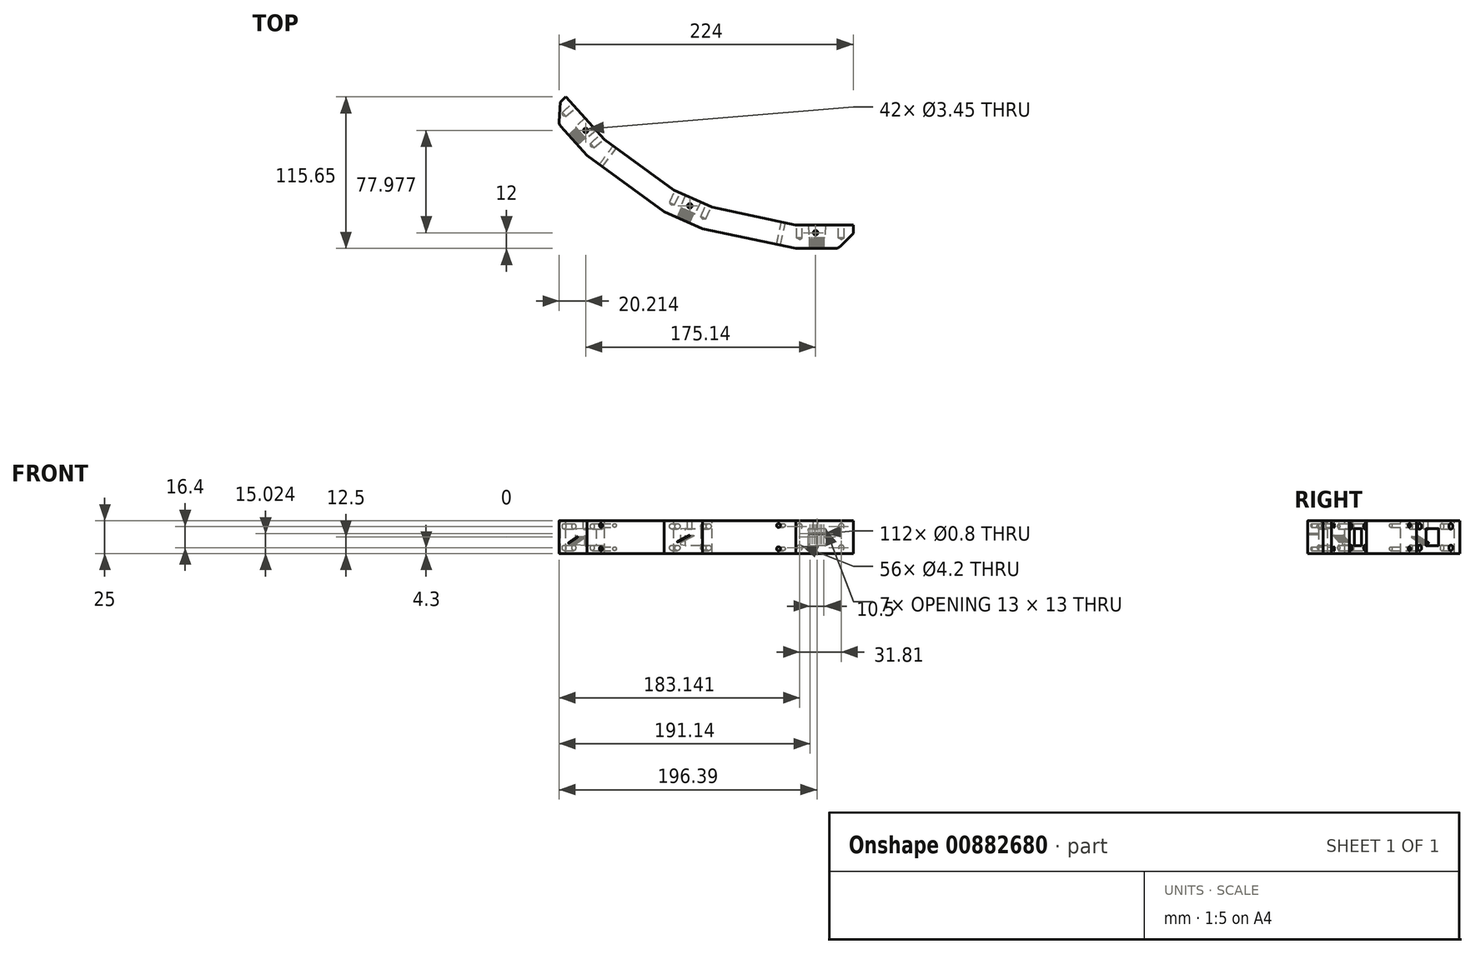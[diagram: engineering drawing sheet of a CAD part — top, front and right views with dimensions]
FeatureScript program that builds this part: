
annotation { "Feature Type Name" : "Feature", "Feature Type Description" : "" }
export const myFeature = defineFeature(function(context is Context, id is Id, definition is map)
    precondition{}
    {
        {
            var Q0;
            Q0=qCreatedBy(makeId("Top.planeOp"),FACE);
            var sketch = newSketch(context, id + "F0", { "sketchPlane" : qUnion([Q0])});
            skCircle(sketch, "E0", {"center": v(0, -260) * mm, "radius": 4.08 * mm});
            skCircle(sketch, "E1", {"center": v(-105.75, -237.52) * mm, "radius": 4.08 * mm});
            skCircle(sketch, "E2", {"center": v(-193.22, -173.97) * mm, "radius": 4.08 * mm});
            skPoint(sketch, "E3", {"position": v(-185.79, -167.28) * mm});
            skPoint(sketch, "E4", {"position": v(-101.68, -228.39) * mm});
            skPoint(sketch, "E5", {"position": v(0, -250) * mm});
            skLineSegment(sketch, "E6.trimOffspring", {"start": v(-104.1, -233.8) * mm, "end": v(-105.75, -237.52) * mm});
            skLineSegment(sketch, "E7.trimOffspring", {"start": v(0, -255.93) * mm, "end": v(0, -260) * mm});
            skLineSegment(sketch, "E8.trimOffspring", {"start": v(-190.19, -171.25) * mm, "end": v(-193.22, -173.97) * mm});
            skLineSegment(sketch, "E9", {"start": v(-185.79, -167.28) * mm, "end": v(-175.08, -179.17) * mm});
            skLineSegment(sketch, "E10", {"start": v(-185.79, -167.28) * mm, "end": v(-195.1, -156.93) * mm});
            skLineSegment(sketch, "E11", {"start": v(-101.68, -228.39) * mm, "end": v(-116.3, -221.88) * mm});
            skLineSegment(sketch, "E12", {"start": v(-101.68, -228.39) * mm, "end": v(-87.07, -234.9) * mm});
            skLineSegment(sketch, "E13", {"start": v(0, -250) * mm, "end": v(-16, -250) * mm});
            skLineSegment(sketch, "E14", {"start": v(0, -250) * mm, "end": v(13.93, -250) * mm});
            skLineSegment(sketch, "E15", {"start": v(-175.08, -179.17) * mm, "end": v(-116.3, -221.88) * mm});
            skLineSegment(sketch, "E16", {"start": v(-87.07, -234.9) * mm, "end": v(-16, -250) * mm});
            skLineSegment(sketch, "E17", {"start": v(-196.38, -153.32) * mm, "end": v(-195.6, -138.3) * mm});
            skLineSegment(sketch, "E18", {"start": v(17.46, -248.54) * mm, "end": v(27.61, -238.39) * mm});
            skPoint(sketch, "E19", {"position": v(-196.5, -155.4) * mm});
            skPoint(sketch, "E20", {"position": v(-172.4, -155.24) * mm});
            skLineSegment(sketch, "E21", {"start": v(-172.4, -155.24) * mm, "end": v(-191.22, -134.35) * mm});
            skLineSegment(sketch, "E22", {"start": v(-195.6, -138.3) * mm, "end": v(-191.22, -134.35) * mm});
            skPoint(sketch, "E23", {"position": v(-94.36, -211.94) * mm});
            skLineSegment(sketch, "E24", {"start": v(-94.36, -211.94) * mm, "end": v(-108.98, -205.43) * mm});
            skLineSegment(sketch, "E25", {"start": v(-172.4, -155.24) * mm, "end": v(-161.7, -167.13) * mm});
            skLineSegment(sketch, "E26", {"start": v(-161.7, -167.13) * mm, "end": v(-108.98, -205.43) * mm});
            skLineSegment(sketch, "E27", {"start": v(-94.36, -211.94) * mm, "end": v(-79.75, -218.45) * mm});
            skPoint(sketch, "E28", {"position": v(-0.5, -232) * mm});
            skLineSegment(sketch, "E29", {"start": v(-0.5, -232) * mm, "end": v(27.61, -232) * mm});
            skLineSegment(sketch, "E30", {"start": v(27.61, -238.39) * mm, "end": v(27.61, -232) * mm});
            skLineSegment(sketch, "E31", {"start": v(-0.5, -232) * mm, "end": v(-16.5, -232) * mm});
            skLineSegment(sketch, "E32", {"start": v(-79.75, -218.45) * mm, "end": v(-16.5, -232) * mm});
            skPoint(sketch, "E33.start.orphan", {"position": v(0, 0) * mm});
            skArc(sketch, "E34.filletArc", {"start": v(-196.38, -153.32) * mm, "mid": v(-196.1, -155.25) * mm, "end": v(-195.1, -156.93) * mm});
            skPoint(sketch, "E35.visualSharp", {"position": v(16, -250) * mm});
            skArc(sketch, "E35.filletArc", {"start": v(13.93, -250) * mm, "mid": v(15.84, -249.62) * mm, "end": v(17.46, -248.54) * mm});
            skSolve(sketch);
        }
        {
            var Q0;
            Q0=makeQuery(id+"F0.imprint","IMPRINT",FACE,{"disambiguationData":[TD([[makeQuery(id+"F0.imprint","IMPRINT",EDGE,{"derivedFrom":sQuery(id+"F0.wireOp",EDGE,"E9")}),1.0]])]});
            extrude(context, id + "F1", {"entities" : qUnion([Q0]), "oppositeDirection" : true, "depth" : 25 * mm, "offsetDistance" : 25 * mm});
        }
        {
            var Q0;
            Q0=makeQuery(id+"F1.opExtrude","SWEPT_FACE",FACE,{"disambiguationData":[OSD([sQuery(id+"F0.wireOp",EDGE,"E24"),sQuery(id+"F0.wireOp",EDGE,"E27")])]});
            var sketch = newSketch(context, id + "F2", { "sketchPlane" : qUnion([Q0])});
            skPoint(sketch, "E36", {"position": v(0, -12.5) * mm});
            skLineSegment(sketch, "E37.bottom", {"start": v(6.5, -19) * mm, "end": v(-6.5, -19) * mm});
            skLineSegment(sketch, "E37.top", {"start": v(6.5, -6) * mm, "end": v(-6.5, -6) * mm});
            skLineSegment(sketch, "E37.left", {"start": v(6.5, -19) * mm, "end": v(6.5, -6) * mm});
            skLineSegment(sketch, "E37.right", {"start": v(-6.5, -19) * mm, "end": v(-6.5, -6) * mm});
            skSolve(sketch);
        }
        {
            var Q0;
            Q0=makeQuery(id+"F2.imprint","IMPRINT",FACE,{"disambiguationData":[TD([[makeQuery(id+"F2.imprint","IMPRINT",EDGE,{"derivedFrom":sQuery(id+"F2.wireOp",EDGE,"E37.bottom")}),-1.0]])]});
            extrude(context, id + "F3", {"entities" : qUnion([Q0]), "operationType" : NewBodyOperationType.REMOVE, "oppositeDirection" : true, "depth" : 10 * mm, "offsetDistance" : 25 * mm, "hasDraft" : true, "draftAngle" : 3 * degree, "draftPullDirection" : true});
        }
        {
            var Q0;
            Q0=makeQuery(id+"F1.opExtrude","SWEPT_FACE",FACE,{"disambiguationData":[OSD([sQuery(id+"F0.wireOp",EDGE,"E21"),sQuery(id+"F0.wireOp",EDGE,"E25")])]});
            var sketch = newSketch(context, id + "F4", { "sketchPlane" : qUnion([Q0])});
            skPoint(sketch, "E38.middle", {"position": v(0, -12.5) * mm});
            skLineSegment(sketch, "E39.bottom", {"start": v(6.5, -19) * mm, "end": v(-6.5, -19) * mm});
            skLineSegment(sketch, "E39.top", {"start": v(6.5, -6) * mm, "end": v(-6.5, -6) * mm});
            skLineSegment(sketch, "E39.left", {"start": v(6.5, -19) * mm, "end": v(6.5, -6) * mm});
            skLineSegment(sketch, "E39.right", {"start": v(-6.5, -19) * mm, "end": v(-6.5, -6) * mm});
            skSolve(sketch);
        }
        {
            var Q0;
            Q0=makeQuery(id+"F4.imprint","IMPRINT",FACE,{"disambiguationData":[TD([[makeQuery(id+"F4.imprint","IMPRINT",EDGE,{"derivedFrom":sQuery(id+"F4.wireOp",EDGE,"E39.bottom")}),-1.0]])]});
            extrude(context, id + "F5", {"entities" : qUnion([Q0]), "operationType" : NewBodyOperationType.REMOVE, "oppositeDirection" : true, "depth" : 10 * mm, "offsetDistance" : 25 * mm, "hasDraft" : true, "draftAngle" : 3 * degree, "draftPullDirection" : true});
        }
        {
            var Q0;
            Q0=makeQuery(id+"F5.boolean.opBoolean","COPY",FACE,{"derivedFrom":makeQuery(id+"F5.opExtrude","CAP_FACE",FACE,{"disambiguationData":[OSD([sQuery(id+"F4.wireOp",EDGE,"E39.bottom"),sQuery(id+"F4.wireOp",EDGE,"E39.top"),sQuery(id+"F4.wireOp",EDGE,"E39.left"),sQuery(id+"F4.wireOp",EDGE,"E39.right")])],"isStart":false})});
            var sketch = newSketch(context, id + "F6", { "sketchPlane" : qUnion([Q0])});
            skLineSegment(sketch, "E40", {"start": v(0, -14.7) * mm, "end": v(6.8, -17.86) * mm});
            skLineSegment(sketch, "E41", {"start": v(0, -14.7) * mm, "end": v(-6.8, -11.53) * mm});
            skPoint(sketch, "E42", {"position": v(0.68, -15.01) * mm});
            skPoint(sketch, "E43", {"position": v(2.04, -15.65) * mm});
            skPoint(sketch, "E44", {"position": v(3.4, -16.28) * mm});
            skPoint(sketch, "E45", {"position": v(4.76, -16.91) * mm});
            skPoint(sketch, "E46", {"position": v(-0.68, -14.38) * mm});
            skPoint(sketch, "E47", {"position": v(-2.04, -13.74) * mm});
            skPoint(sketch, "E48", {"position": v(-3.4, -13.1) * mm});
            skPoint(sketch, "E49", {"position": v(-4.76, -12.48) * mm});
            skLineSegment(sketch, "E50", {"start": v(-4.76, -12.48) * mm, "end": v(-4.76, -18.48) * mm});
            skSolve(sketch);
        }
        {
            var Q0;
            Q0=sQuery(id+"F6.wireOp",VERTEX,"E45");
            var Q1;
            Q1=sQuery(id+"F6.wireOp",VERTEX,"E44");
            var Q2;
            Q2=sQuery(id+"F6.wireOp",VERTEX,"E43");
            var Q3;
            Q3=sQuery(id+"F6.wireOp",VERTEX,"E42");
            var Q4;
            Q4=sQuery(id+"F6.wireOp",VERTEX,"E46");
            var Q5;
            Q5=sQuery(id+"F6.wireOp",VERTEX,"E47");
            var Q6;
            Q6=sQuery(id+"F6.wireOp",VERTEX,"E48");
            var Q7;
            Q7=sQuery(id+"F6.wireOp",VERTEX,"E49");
            var Q8;
            Q8=makeQuery(id+"F1.opExtrude","SWEPT_BODY",BODY,{"disambiguationData":[OSD([sQuery(id+"F0.wireOp",EDGE,"E9"),sQuery(id+"F0.wireOp",EDGE,"E10"),sQuery(id+"F0.wireOp",EDGE,"E11"),sQuery(id+"F0.wireOp",EDGE,"E12"),sQuery(id+"F0.wireOp",EDGE,"E13"),sQuery(id+"F0.wireOp",EDGE,"E14"),sQuery(id+"F0.wireOp",EDGE,"E15"),sQuery(id+"F0.wireOp",EDGE,"E16"),sQuery(id+"F0.wireOp",EDGE,"E17"),sQuery(id+"F0.wireOp",EDGE,"E18"),sQuery(id+"F0.wireOp",EDGE,"E21"),sQuery(id+"F0.wireOp",EDGE,"E22"),sQuery(id+"F0.wireOp",EDGE,"E24"),sQuery(id+"F0.wireOp",EDGE,"E25"),sQuery(id+"F0.wireOp",EDGE,"E26"),sQuery(id+"F0.wireOp",EDGE,"E27"),sQuery(id+"F0.wireOp",EDGE,"E29"),sQuery(id+"F0.wireOp",EDGE,"E30"),sQuery(id+"F0.wireOp",EDGE,"E31"),sQuery(id+"F0.wireOp",EDGE,"E32"),sQuery(id+"F0.wireOp",EDGE,"E34.filletArc"),sQuery(id+"F0.wireOp",EDGE,"E35.filletArc")])]});
            hole(context, id + "F7", {"style" : HoleStyle.C_SINK, "endStyle" : HoleEndStyle.THROUGH, "holeDiameter" : 0.8 * mm, "cSinkDiameter" : 0.87 * mm, "cSinkAngle" : 60 * degree, "majorDiameter" : 5 * mm, "isTappedThrough" : true, "tappedDepth" : 12 * mm, "tapClearance" : 3, "locations" : qUnion([Q0, Q1, Q2, Q3, Q4, Q5, Q6, Q7]), "scope" : qUnion([Q8])});
        }
        {
            var Q0;
            Q0=makeQuery(id+"F3.boolean.opBoolean","COPY",FACE,{"derivedFrom":makeQuery(id+"F3.opExtrude","CAP_FACE",FACE,{"disambiguationData":[OSD([sQuery(id+"F2.wireOp",EDGE,"E37.bottom"),sQuery(id+"F2.wireOp",EDGE,"E37.top"),sQuery(id+"F2.wireOp",EDGE,"E37.left"),sQuery(id+"F2.wireOp",EDGE,"E37.right")])],"isStart":false})});
            var sketch = newSketch(context, id + "F8", { "sketchPlane" : qUnion([Q0])});
            skLineSegment(sketch, "E51", {"start": v(0, -13.7) * mm, "end": v(5.15, -16.1) * mm});
            skLineSegment(sketch, "E52", {"start": v(0, -13.7) * mm, "end": v(-6.8, -10.53) * mm});
            skPoint(sketch, "E53", {"position": v(0.68, -14.01) * mm});
            skPoint(sketch, "E54", {"position": v(2.04, -14.65) * mm});
            skPoint(sketch, "E55", {"position": v(3.4, -15.28) * mm});
            skPoint(sketch, "E56", {"position": v(-0.68, -13.38) * mm});
            skPoint(sketch, "E57", {"position": v(-2.04, -12.74) * mm});
            skPoint(sketch, "E58", {"position": v(-3.4, -12.1) * mm});
            skPoint(sketch, "E59", {"position": v(4.76, -15.91) * mm});
            skPoint(sketch, "E60", {"position": v(-4.76, -11.48) * mm});
            skLineSegment(sketch, "E61", {"start": v(-4.76, -11.48) * mm, "end": v(-4.76, -18.48) * mm});
            skSolve(sketch);
        }
        {
            var Q0;
            Q0=sQuery(id+"F8.wireOp",VERTEX,"E59");
            var Q1;
            Q1=sQuery(id+"F8.wireOp",VERTEX,"E55");
            var Q2;
            Q2=sQuery(id+"F8.wireOp",VERTEX,"E54");
            var Q3;
            Q3=sQuery(id+"F8.wireOp",VERTEX,"E53");
            var Q4;
            Q4=sQuery(id+"F8.wireOp",VERTEX,"E56");
            var Q5;
            Q5=sQuery(id+"F8.wireOp",VERTEX,"E57");
            var Q6;
            Q6=sQuery(id+"F8.wireOp",VERTEX,"E58");
            var Q7;
            Q7=sQuery(id+"F8.wireOp",VERTEX,"E60");
            var Q8;
            Q8=makeQuery(id+"F1.opExtrude","SWEPT_BODY",BODY,{"disambiguationData":[OSD([sQuery(id+"F0.wireOp",EDGE,"E9"),sQuery(id+"F0.wireOp",EDGE,"E10"),sQuery(id+"F0.wireOp",EDGE,"E11"),sQuery(id+"F0.wireOp",EDGE,"E12"),sQuery(id+"F0.wireOp",EDGE,"E13"),sQuery(id+"F0.wireOp",EDGE,"E14"),sQuery(id+"F0.wireOp",EDGE,"E15"),sQuery(id+"F0.wireOp",EDGE,"E16"),sQuery(id+"F0.wireOp",EDGE,"E17"),sQuery(id+"F0.wireOp",EDGE,"E18"),sQuery(id+"F0.wireOp",EDGE,"E21"),sQuery(id+"F0.wireOp",EDGE,"E22"),sQuery(id+"F0.wireOp",EDGE,"E24"),sQuery(id+"F0.wireOp",EDGE,"E25"),sQuery(id+"F0.wireOp",EDGE,"E26"),sQuery(id+"F0.wireOp",EDGE,"E27"),sQuery(id+"F0.wireOp",EDGE,"E29"),sQuery(id+"F0.wireOp",EDGE,"E30"),sQuery(id+"F0.wireOp",EDGE,"E31"),sQuery(id+"F0.wireOp",EDGE,"E32"),sQuery(id+"F0.wireOp",EDGE,"E34.filletArc"),sQuery(id+"F0.wireOp",EDGE,"E35.filletArc")])]});
            hole(context, id + "F9", {"style" : HoleStyle.C_SINK, "endStyle" : HoleEndStyle.THROUGH, "holeDiameter" : 0.8 * mm, "cSinkDiameter" : 0.87 * mm, "cSinkAngle" : 60 * degree, "majorDiameter" : 5 * mm, "isTappedThrough" : true, "tappedDepth" : 12 * mm, "tapClearance" : 3, "locations" : qUnion([Q0, Q1, Q2, Q3, Q4, Q5, Q6, Q7]), "scope" : qUnion([Q8])});
        }
        {
            var Q0;
            Q0=makeQuery(id+"F1.opExtrude","SWEPT_FACE",FACE,{"disambiguationData":[OSD([sQuery(id+"F0.wireOp",EDGE,"E29"),sQuery(id+"F0.wireOp",EDGE,"E31")])]});
            var sketch = newSketch(context, id + "F10", { "sketchPlane" : qUnion([Q0])});
            skLineSegment(sketch, "E62.bottom", {"start": v(6.5, -19) * mm, "end": v(-6.5, -19) * mm});
            skLineSegment(sketch, "E62.top", {"start": v(6.5, -6) * mm, "end": v(-6.5, -6) * mm});
            skLineSegment(sketch, "E62.left", {"start": v(6.5, -19) * mm, "end": v(6.5, -6) * mm});
            skLineSegment(sketch, "E62.right", {"start": v(-6.5, -19) * mm, "end": v(-6.5, -6) * mm});
            skPoint(sketch, "E62.middle", {"position": v(0, -12.5) * mm});
            skSolve(sketch);
        }
        {
            var Q0;
            Q0=makeQuery(id+"F10.imprint","IMPRINT",FACE,{"disambiguationData":[TD([[makeQuery(id+"F10.imprint","IMPRINT",EDGE,{"derivedFrom":sQuery(id+"F10.wireOp",EDGE,"E62.bottom")}),-1.0]])]});
            extrude(context, id + "F11", {"entities" : qUnion([Q0]), "operationType" : NewBodyOperationType.REMOVE, "oppositeDirection" : true, "depth" : 10 * mm, "offsetDistance" : 25 * mm, "hasDraft" : true, "draftAngle" : 3 * degree, "draftPullDirection" : true});
        }
        {
            var Q0;
            Q0=makeQuery(id+"F11.boolean.opBoolean","COPY",FACE,{"derivedFrom":makeQuery(id+"F11.opExtrude","CAP_FACE",FACE,{"disambiguationData":[OSD([sQuery(id+"F10.wireOp",EDGE,"E62.bottom"),sQuery(id+"F10.wireOp",EDGE,"E62.top"),sQuery(id+"F10.wireOp",EDGE,"E62.left"),sQuery(id+"F10.wireOp",EDGE,"E62.right")])],"isStart":false})});
            var sketch = newSketch(context, id + "F12", { "sketchPlane" : qUnion([Q0])});
            skLineSegment(sketch, "E63", {"start": v(0, -18.48) * mm, "end": v(0, -9.98) * mm});
            skPoint(sketch, "E64", {"position": v(0.75, -9.98) * mm});
            skPoint(sketch, "E65", {"position": v(2.25, -9.98) * mm});
            skPoint(sketch, "E66", {"position": v(3.75, -9.98) * mm});
            skPoint(sketch, "E67", {"position": v(5.25, -9.98) * mm});
            skPoint(sketch, "E68", {"position": v(-0.75, -9.98) * mm});
            skPoint(sketch, "E69", {"position": v(-2.25, -9.98) * mm});
            skPoint(sketch, "E70", {"position": v(-3.75, -9.98) * mm});
            skPoint(sketch, "E71", {"position": v(-5.25, -9.98) * mm});
            skSolve(sketch);
        }
        {
            var Q0;
            Q0=sQuery(id+"F12.wireOp",VERTEX,"E67");
            var Q1;
            Q1=sQuery(id+"F12.wireOp",VERTEX,"E66");
            var Q2;
            Q2=sQuery(id+"F12.wireOp",VERTEX,"E65");
            var Q3;
            Q3=sQuery(id+"F12.wireOp",VERTEX,"E64");
            var Q4;
            Q4=sQuery(id+"F12.wireOp",VERTEX,"E68");
            var Q5;
            Q5=sQuery(id+"F12.wireOp",VERTEX,"E69");
            var Q6;
            Q6=sQuery(id+"F12.wireOp",VERTEX,"E70");
            var Q7;
            Q7=sQuery(id+"F12.wireOp",VERTEX,"E71");
            var Q8;
            Q8=makeQuery(id+"F1.opExtrude","SWEPT_BODY",BODY,{"disambiguationData":[OSD([sQuery(id+"F0.wireOp",EDGE,"E9"),sQuery(id+"F0.wireOp",EDGE,"E10"),sQuery(id+"F0.wireOp",EDGE,"E11"),sQuery(id+"F0.wireOp",EDGE,"E12"),sQuery(id+"F0.wireOp",EDGE,"E13"),sQuery(id+"F0.wireOp",EDGE,"E14"),sQuery(id+"F0.wireOp",EDGE,"E15"),sQuery(id+"F0.wireOp",EDGE,"E16"),sQuery(id+"F0.wireOp",EDGE,"E17"),sQuery(id+"F0.wireOp",EDGE,"E18"),sQuery(id+"F0.wireOp",EDGE,"E21"),sQuery(id+"F0.wireOp",EDGE,"E22"),sQuery(id+"F0.wireOp",EDGE,"E24"),sQuery(id+"F0.wireOp",EDGE,"E25"),sQuery(id+"F0.wireOp",EDGE,"E26"),sQuery(id+"F0.wireOp",EDGE,"E27"),sQuery(id+"F0.wireOp",EDGE,"E29"),sQuery(id+"F0.wireOp",EDGE,"E30"),sQuery(id+"F0.wireOp",EDGE,"E31"),sQuery(id+"F0.wireOp",EDGE,"E32"),sQuery(id+"F0.wireOp",EDGE,"E34.filletArc"),sQuery(id+"F0.wireOp",EDGE,"E35.filletArc")])]});
            hole(context, id + "F13", {"style" : HoleStyle.C_SINK, "endStyle" : HoleEndStyle.THROUGH, "holeDiameter" : 0.8 * mm, "cSinkDiameter" : 0.87 * mm, "cSinkAngle" : 60 * degree, "majorDiameter" : 5 * mm, "isTappedThrough" : true, "tappedDepth" : 12 * mm, "tapClearance" : 3, "locations" : qUnion([Q0, Q1, Q2, Q3, Q4, Q5, Q6, Q7]), "scope" : qUnion([Q8])});
        }
        {
            var Q0;
            Q0=makeQuery(id+"F1.opExtrude","CAP_FACE",FACE,{"disambiguationData":[OSD([sQuery(id+"F0.wireOp",EDGE,"E9"),sQuery(id+"F0.wireOp",EDGE,"E10"),sQuery(id+"F0.wireOp",EDGE,"E11"),sQuery(id+"F0.wireOp",EDGE,"E12"),sQuery(id+"F0.wireOp",EDGE,"E13"),sQuery(id+"F0.wireOp",EDGE,"E14"),sQuery(id+"F0.wireOp",EDGE,"E15"),sQuery(id+"F0.wireOp",EDGE,"E16"),sQuery(id+"F0.wireOp",EDGE,"E17"),sQuery(id+"F0.wireOp",EDGE,"E18"),sQuery(id+"F0.wireOp",EDGE,"E21"),sQuery(id+"F0.wireOp",EDGE,"E22"),sQuery(id+"F0.wireOp",EDGE,"E24"),sQuery(id+"F0.wireOp",EDGE,"E25"),sQuery(id+"F0.wireOp",EDGE,"E26"),sQuery(id+"F0.wireOp",EDGE,"E27"),sQuery(id+"F0.wireOp",EDGE,"E29"),sQuery(id+"F0.wireOp",EDGE,"E30"),sQuery(id+"F0.wireOp",EDGE,"E31"),sQuery(id+"F0.wireOp",EDGE,"E32"),sQuery(id+"F0.wireOp",EDGE,"E34.filletArc"),sQuery(id+"F0.wireOp",EDGE,"E35.filletArc")])],"isStart":true});
            var sketch = newSketch(context, id + "F14", { "sketchPlane" : qUnion([Q0])});
            skLineSegment(sketch, "E72", {"start": v(-94.36, -211.94) * mm, "end": v(-101.68, -228.39) * mm});
            skLineSegment(sketch, "E73", {"start": v(-185.1, -168.05) * mm, "end": v(-171.72, -156) * mm});
            skLineSegment(sketch, "E74", {"start": v(-1.04, -250) * mm, "end": v(-1.04, -232) * mm});
            skPoint(sketch, "E75", {"position": v(-1.04, -238) * mm});
            skPoint(sketch, "E76", {"position": v(-96.8, -217.42) * mm});
            skPoint(sketch, "E77", {"position": v(-176.18, -160.02) * mm});
            skSolve(sketch);
        }
        {
            var Q0;
            Q0=sQuery(id+"F14.wireOp",VERTEX,"E77");
            var Q1;
            Q1=sQuery(id+"F14.wireOp",VERTEX,"E76");
            var Q2;
            Q2=sQuery(id+"F14.wireOp",VERTEX,"E75");
            var Q3;
            Q3=makeQuery(id+"F1.opExtrude","SWEPT_BODY",BODY,{"disambiguationData":[OSD([sQuery(id+"F0.wireOp",EDGE,"E9"),sQuery(id+"F0.wireOp",EDGE,"E10"),sQuery(id+"F0.wireOp",EDGE,"E11"),sQuery(id+"F0.wireOp",EDGE,"E12"),sQuery(id+"F0.wireOp",EDGE,"E13"),sQuery(id+"F0.wireOp",EDGE,"E14"),sQuery(id+"F0.wireOp",EDGE,"E15"),sQuery(id+"F0.wireOp",EDGE,"E16"),sQuery(id+"F0.wireOp",EDGE,"E17"),sQuery(id+"F0.wireOp",EDGE,"E18"),sQuery(id+"F0.wireOp",EDGE,"E21"),sQuery(id+"F0.wireOp",EDGE,"E22"),sQuery(id+"F0.wireOp",EDGE,"E24"),sQuery(id+"F0.wireOp",EDGE,"E25"),sQuery(id+"F0.wireOp",EDGE,"E26"),sQuery(id+"F0.wireOp",EDGE,"E27"),sQuery(id+"F0.wireOp",EDGE,"E29"),sQuery(id+"F0.wireOp",EDGE,"E30"),sQuery(id+"F0.wireOp",EDGE,"E31"),sQuery(id+"F0.wireOp",EDGE,"E32"),sQuery(id+"F0.wireOp",EDGE,"E34.filletArc"),sQuery(id+"F0.wireOp",EDGE,"E35.filletArc")])]});
            hole(context, id + "F15", {"style" : HoleStyle.SIMPLE, "endStyle" : HoleEndStyle.BLIND, "standardTappedOrClearance" : lookupTablePath({ "standard" : "ANSI", "engagement" : "75%", "pitch" : "32 tpi", "size" : "#8", "type" : "Tapped" }), "standardBlindInLast" : lookupTablePath({ "standard" : "ANSI", "engagement" : "75%", "pitch" : "32 tpi", "size" : "#8", "type" : "Tapped" }), "holeDiameter" : 3.45 * mm, "majorDiameter" : 4.17 * mm, "showTappedDepth" : true, "holeDepth" : 14.38 * mm, "isTappedThrough" : true, "tappedDepth" : 12 * mm, "tapClearance" : 3, "locations" : qUnion([Q0, Q1, Q2]), "scope" : qUnion([Q3])});
        }
        {
            var Q0;
            {var subQ3=sQuery(id+"F0.wireOp",EDGE,"E31");var subQ4=sQuery(id+"F0.wireOp",EDGE,"E30");var subQ5=sQuery(id+"F0.wireOp",EDGE,"E29");Q0=makeQuery(id+"Fe6iQ39P3XZATja_1.boolean.opBoolean","SPLIT",FACE,{"disambiguationData":[TD([makeQuery(id+"F1.opExtrude","SWEPT_FACE",FACE,{"disambiguationData":[OSD([subQ4])]})])],"derivedFrom":makeQuery(id+"F1.opExtrude","SWEPT_FACE",FACE,{"disambiguationData":[OSD([subQ5,subQ3])]})});}
            var sketch = newSketch(context, id + "F16", { "sketchPlane" : qUnion([Q0])});
            skLineSegment(sketch, "E78", {"start": v(-18.56, -4.3) * mm, "end": v(-27.61, -4.3) * mm});
            skLineSegment(sketch, "E79", {"start": v(-18.56, -20.7) * mm, "end": v(-27.61, -20.7) * mm});
            skPoint(sketch, "E80", {"position": v(13.25, -4.3) * mm});
            skPoint(sketch, "E81", {"position": v(13.25, -20.7) * mm});
            skPoint(sketch, "E82", {"position": v(-18.56, -4.3) * mm});
            skPoint(sketch, "E83", {"position": v(-18.56, -20.7) * mm});
            skSolve(sketch);
        }
        {
            var Q0;
            Q0=sQuery(id+"F16.wireOp",VERTEX,"960df98d-92ac-47f4-9385-bcb4d4738518");
            var Q1;
            Q1=sQuery(id+"F16.wireOp",VERTEX,"E80");
            var Q2;
            Q2=sQuery(id+"F16.wireOp",VERTEX,"E81");
            var Q3;
            Q3=sQuery(id+"F16.wireOp",VERTEX,"70c8c2b4-ec63-4f9a-a490-eeb2e280e894");
            var Q4;
            Q4=sQuery(id+"F16.wireOp",VERTEX,"E82");
            var Q5;
            Q5=sQuery(id+"F16.wireOp",VERTEX,"E83");
            var Q6;
            Q6=makeQuery(id+"F1.opExtrude","SWEPT_BODY",BODY,{"disambiguationData":[OSD([sQuery(id+"F0.wireOp",EDGE,"E9"),sQuery(id+"F0.wireOp",EDGE,"E10"),sQuery(id+"F0.wireOp",EDGE,"E11"),sQuery(id+"F0.wireOp",EDGE,"E12"),sQuery(id+"F0.wireOp",EDGE,"E13"),sQuery(id+"F0.wireOp",EDGE,"E14"),sQuery(id+"F0.wireOp",EDGE,"E15"),sQuery(id+"F0.wireOp",EDGE,"E16"),sQuery(id+"F0.wireOp",EDGE,"E17"),sQuery(id+"F0.wireOp",EDGE,"E18"),sQuery(id+"F0.wireOp",EDGE,"E21"),sQuery(id+"F0.wireOp",EDGE,"E22"),sQuery(id+"F0.wireOp",EDGE,"E24"),sQuery(id+"F0.wireOp",EDGE,"E25"),sQuery(id+"F0.wireOp",EDGE,"E26"),sQuery(id+"F0.wireOp",EDGE,"E27"),sQuery(id+"F0.wireOp",EDGE,"E29"),sQuery(id+"F0.wireOp",EDGE,"E30"),sQuery(id+"F0.wireOp",EDGE,"E31"),sQuery(id+"F0.wireOp",EDGE,"E32"),sQuery(id+"F0.wireOp",EDGE,"E34.filletArc"),sQuery(id+"F0.wireOp",EDGE,"E35.filletArc")])]});
            hole(context, id + "F17", {"style" : HoleStyle.SIMPLE, "endStyle" : HoleEndStyle.BLIND, "standardTappedOrClearance" : lookupTablePath({ "standard" : "ISO", "engagement" : "75%", "pitch" : "0.8 mm", "size" : "M5", "type" : "Tapped" }), "standardBlindInLast" : lookupTablePath({ "standard" : "ISO", "engagement" : "75%", "pitch" : "0.8 mm", "size" : "M5", "type" : "Tapped" }), "holeDiameter" : 4.2 * mm, "majorDiameter" : 5 * mm, "showTappedDepth" : true, "holeDepth" : 10 * mm, "isTappedThrough" : true, "tappedDepth" : 7.6 * mm, "tapClearance" : 3, "locations" : qUnion([Q0, Q1, Q2, Q3, Q4, Q5]), "scope" : qUnion([Q6])});
        }
        {
            var Q0;
            Q0=makeQuery(id+"F11.boolean.opBoolean","COPY",EDGE,{"derivedFrom":makeQuery(id+"F11.opExtrude","CAP_EDGE",EDGE,{"disambiguationData":[OSD([sQuery(id+"F10.wireOp",EDGE,"E62.left")])],"isStart":false})});
            var Q1;
            Q1=makeQuery(id+"F11.boolean.opBoolean","COPY",EDGE,{"derivedFrom":makeQuery(id+"F11.opExtrude","CAP_EDGE",EDGE,{"disambiguationData":[OSD([sQuery(id+"F10.wireOp",EDGE,"E62.top")])],"isStart":false})});
            var Q2;
            Q2=makeQuery(id+"F11.boolean.opBoolean","COPY",EDGE,{"derivedFrom":makeQuery(id+"F11.opExtrude","CAP_EDGE",EDGE,{"disambiguationData":[OSD([sQuery(id+"F10.wireOp",EDGE,"E62.right")])],"isStart":false})});
            var Q3;
            Q3=makeQuery(id+"F11.boolean.opBoolean","COPY",EDGE,{"derivedFrom":makeQuery(id+"F11.opExtrude","CAP_EDGE",EDGE,{"disambiguationData":[OSD([sQuery(id+"F10.wireOp",EDGE,"E62.bottom")])],"isStart":false})});
            var Q4;
            Q4=makeQuery(id+"F11.boolean.opBoolean","COPY",EDGE,{"derivedFrom":makeQuery(id+"F11.opExtrude","SWEPT_EDGE",EDGE,{"disambiguationData":[OSD([sQuery(id+"F10.wireOp",EDGE,"E62.top"),sQuery(id+"F10.wireOp",EDGE,"E62.left")])]})});
            var Q5;
            Q5=makeQuery(id+"F11.boolean.opBoolean","COPY",EDGE,{"derivedFrom":makeQuery(id+"F11.opExtrude","SWEPT_EDGE",EDGE,{"disambiguationData":[OSD([sQuery(id+"F10.wireOp",EDGE,"E62.top"),sQuery(id+"F10.wireOp",EDGE,"E62.right")])]})});
            var Q6;
            Q6=makeQuery(id+"F11.boolean.opBoolean","COPY",EDGE,{"derivedFrom":makeQuery(id+"F11.opExtrude","SWEPT_EDGE",EDGE,{"disambiguationData":[OSD([sQuery(id+"F10.wireOp",EDGE,"E62.bottom"),sQuery(id+"F10.wireOp",EDGE,"E62.right")])]})});
            fillet(context, id + "F18", {"entities" : qUnion([Q0, Q1, Q2, Q3, Q4, Q5, Q6]), "radius" : 0.3 * mm, "tangentPropagation" : true, "allowEdgeOverflow" : false});
        }
        {
            var Q0;
            Q0=makeQuery(id+"F3.boolean.opBoolean","COPY",EDGE,{"derivedFrom":makeQuery(id+"F3.opExtrude","CAP_EDGE",EDGE,{"disambiguationData":[OSD([sQuery(id+"F2.wireOp",EDGE,"E37.top")])],"isStart":false})});
            var Q1;
            Q1=makeQuery(id+"F3.boolean.opBoolean","COPY",EDGE,{"derivedFrom":makeQuery(id+"F3.opExtrude","CAP_EDGE",EDGE,{"disambiguationData":[OSD([sQuery(id+"F2.wireOp",EDGE,"E37.right")])],"isStart":false})});
            var Q2;
            Q2=makeQuery(id+"F3.boolean.opBoolean","COPY",EDGE,{"derivedFrom":makeQuery(id+"F3.opExtrude","SWEPT_EDGE",EDGE,{"disambiguationData":[OSD([sQuery(id+"F2.wireOp",EDGE,"E37.top"),sQuery(id+"F2.wireOp",EDGE,"E37.right")])]})});
            var Q3;
            Q3=makeQuery(id+"F3.boolean.opBoolean","COPY",EDGE,{"derivedFrom":makeQuery(id+"F3.opExtrude","SWEPT_EDGE",EDGE,{"disambiguationData":[OSD([sQuery(id+"F2.wireOp",EDGE,"E37.bottom"),sQuery(id+"F2.wireOp",EDGE,"E37.right")])]})});
            var Q4;
            Q4=makeQuery(id+"F3.boolean.opBoolean","COPY",EDGE,{"derivedFrom":makeQuery(id+"F3.opExtrude","CAP_EDGE",EDGE,{"disambiguationData":[OSD([sQuery(id+"F2.wireOp",EDGE,"E37.bottom")])],"isStart":false})});
            var Q5;
            Q5=makeQuery(id+"F3.boolean.opBoolean","COPY",EDGE,{"derivedFrom":makeQuery(id+"F3.opExtrude","CAP_EDGE",EDGE,{"disambiguationData":[OSD([sQuery(id+"F2.wireOp",EDGE,"E37.left")])],"isStart":false})});
            var Q6;
            Q6=makeQuery(id+"F3.boolean.opBoolean","COPY",EDGE,{"derivedFrom":makeQuery(id+"F3.opExtrude","SWEPT_EDGE",EDGE,{"disambiguationData":[OSD([sQuery(id+"F2.wireOp",EDGE,"E37.top"),sQuery(id+"F2.wireOp",EDGE,"E37.left")])]})});
            var Q7;
            Q7=makeQuery(id+"F3.boolean.opBoolean","COPY",EDGE,{"derivedFrom":makeQuery(id+"F3.opExtrude","SWEPT_EDGE",EDGE,{"disambiguationData":[OSD([sQuery(id+"F2.wireOp",EDGE,"E37.bottom"),sQuery(id+"F2.wireOp",EDGE,"E37.left")])]})});
            fillet(context, id + "F19", {"entities" : qUnion([Q0, Q1, Q2, Q3, Q4, Q5, Q6, Q7]), "radius" : 0.3 * mm, "tangentPropagation" : true, "allowEdgeOverflow" : false});
        }
        {
            var Q0;
            Q0=makeQuery(id+"F5.boolean.opBoolean","COPY",EDGE,{"derivedFrom":makeQuery(id+"F5.opExtrude","CAP_EDGE",EDGE,{"disambiguationData":[OSD([sQuery(id+"F4.wireOp",EDGE,"E39.bottom")])],"isStart":false})});
            var Q1;
            Q1=makeQuery(id+"F5.boolean.opBoolean","COPY",EDGE,{"derivedFrom":makeQuery(id+"F5.opExtrude","CAP_EDGE",EDGE,{"disambiguationData":[OSD([sQuery(id+"F4.wireOp",EDGE,"E39.top")])],"isStart":false})});
            var Q2;
            Q2=makeQuery(id+"F5.boolean.opBoolean","COPY",EDGE,{"derivedFrom":makeQuery(id+"F5.opExtrude","CAP_EDGE",EDGE,{"disambiguationData":[OSD([sQuery(id+"F4.wireOp",EDGE,"E39.right")])],"isStart":false})});
            var Q3;
            Q3=makeQuery(id+"F5.boolean.opBoolean","COPY",EDGE,{"derivedFrom":makeQuery(id+"F5.opExtrude","SWEPT_EDGE",EDGE,{"disambiguationData":[OSD([sQuery(id+"F4.wireOp",EDGE,"E39.top"),sQuery(id+"F4.wireOp",EDGE,"E39.right")])]})});
            var Q4;
            Q4=makeQuery(id+"F5.boolean.opBoolean","COPY",EDGE,{"derivedFrom":makeQuery(id+"F5.opExtrude","SWEPT_EDGE",EDGE,{"disambiguationData":[OSD([sQuery(id+"F4.wireOp",EDGE,"E39.bottom"),sQuery(id+"F4.wireOp",EDGE,"E39.right")])]})});
            var Q5;
            Q5=makeQuery(id+"F5.boolean.opBoolean","COPY",EDGE,{"derivedFrom":makeQuery(id+"F5.opExtrude","CAP_EDGE",EDGE,{"disambiguationData":[OSD([sQuery(id+"F4.wireOp",EDGE,"E39.left")])],"isStart":false})});
            var Q6;
            Q6=makeQuery(id+"F5.boolean.opBoolean","COPY",EDGE,{"derivedFrom":makeQuery(id+"F5.opExtrude","SWEPT_EDGE",EDGE,{"disambiguationData":[OSD([sQuery(id+"F4.wireOp",EDGE,"E39.top"),sQuery(id+"F4.wireOp",EDGE,"E39.left")])]})});
            var Q7;
            Q7=makeQuery(id+"F5.boolean.opBoolean","COPY",EDGE,{"derivedFrom":makeQuery(id+"F5.opExtrude","SWEPT_EDGE",EDGE,{"disambiguationData":[OSD([sQuery(id+"F4.wireOp",EDGE,"E39.bottom"),sQuery(id+"F4.wireOp",EDGE,"E39.left")])]})});
            fillet(context, id + "F20", {"entities" : qUnion([Q0, Q1, Q2, Q3, Q4, Q5, Q6, Q7]), "radius" : 0.3 * mm, "tangentPropagation" : true, "allowEdgeOverflow" : false});
        }
        {
            var Q0;
            {var subQ6=sQuery(id+"F0.wireOp",EDGE,"E27");var subQ7=sQuery(id+"F0.wireOp",EDGE,"E26");var subQ9=sQuery(id+"F0.wireOp",EDGE,"E24");Q0=makeQuery(id+"Fw17XcnKaz8ayvf_1.boolean.opBoolean","SPLIT",FACE,{"disambiguationData":[TD([makeQuery(id+"F1.opExtrude","SWEPT_FACE",FACE,{"disambiguationData":[OSD([subQ7])]})])],"derivedFrom":makeQuery(id+"F1.opExtrude","SWEPT_FACE",FACE,{"disambiguationData":[OSD([subQ9,subQ6])]})});}
            var sketch = newSketch(context, id + "F21", { "sketchPlane" : qUnion([Q0])});
            skPoint(sketch, "E84", {"position": v(-13, -4.3) * mm});
            skPoint(sketch, "E85", {"position": v(-13, -20.7) * mm});
            skPoint(sketch, "E86", {"position": v(13, -4.3) * mm});
            skPoint(sketch, "E87", {"position": v(13, -20.7) * mm});
            skPoint(sketch, "E88.orphan", {"position": v(-10, -4.3) * mm});
            skPoint(sketch, "E89.orphan", {"position": v(10, -4.3) * mm});
            skPoint(sketch, "E90.orphan", {"position": v(-10, -20.7) * mm});
            skPoint(sketch, "E91.orphan", {"position": v(10, -20.7) * mm});
            skPoint(sketch, "E92.end.orphan", {"position": v(16, -4.3) * mm});
            skPoint(sketch, "E93.end.orphan", {"position": v(16, -20.7) * mm});
            skPoint(sketch, "E94.end.orphan", {"position": v(-16, -4.3) * mm});
            skPoint(sketch, "E95.end.orphan", {"position": v(-16, -20.7) * mm});
            skSolve(sketch);
        }
        {
            var Q0;
            Q0=sQuery(id+"F21.wireOp",VERTEX,"E84");
            var Q1;
            Q1=sQuery(id+"F21.wireOp",VERTEX,"E85");
            var Q2;
            Q2=sQuery(id+"F21.wireOp",VERTEX,"E86");
            var Q3;
            Q3=sQuery(id+"F21.wireOp",VERTEX,"E87");
            var Q4;
            Q4=makeQuery(id+"F1.opExtrude","SWEPT_BODY",BODY,{"disambiguationData":[OSD([sQuery(id+"F0.wireOp",EDGE,"E9"),sQuery(id+"F0.wireOp",EDGE,"E10"),sQuery(id+"F0.wireOp",EDGE,"E11"),sQuery(id+"F0.wireOp",EDGE,"E12"),sQuery(id+"F0.wireOp",EDGE,"E13"),sQuery(id+"F0.wireOp",EDGE,"E14"),sQuery(id+"F0.wireOp",EDGE,"E15"),sQuery(id+"F0.wireOp",EDGE,"E16"),sQuery(id+"F0.wireOp",EDGE,"E17"),sQuery(id+"F0.wireOp",EDGE,"E18"),sQuery(id+"F0.wireOp",EDGE,"E21"),sQuery(id+"F0.wireOp",EDGE,"E22"),sQuery(id+"F0.wireOp",EDGE,"E24"),sQuery(id+"F0.wireOp",EDGE,"E25"),sQuery(id+"F0.wireOp",EDGE,"E26"),sQuery(id+"F0.wireOp",EDGE,"E27"),sQuery(id+"F0.wireOp",EDGE,"E29"),sQuery(id+"F0.wireOp",EDGE,"E30"),sQuery(id+"F0.wireOp",EDGE,"E31"),sQuery(id+"F0.wireOp",EDGE,"E32"),sQuery(id+"F0.wireOp",EDGE,"E34.filletArc"),sQuery(id+"F0.wireOp",EDGE,"E35.filletArc")])]});
            hole(context, id + "F22", {"style" : HoleStyle.SIMPLE, "endStyle" : HoleEndStyle.BLIND, "standardTappedOrClearance" : lookupTablePath({ "standard" : "ISO", "engagement" : "75%", "pitch" : "0.8 mm", "size" : "M5", "type" : "Tapped" }), "standardBlindInLast" : lookupTablePath({ "standard" : "ISO", "engagement" : "75%", "pitch" : "0.8 mm", "size" : "M5", "type" : "Tapped" }), "holeDiameter" : 4.2 * mm, "majorDiameter" : 5 * mm, "showTappedDepth" : true, "holeDepth" : 10 * mm, "isTappedThrough" : true, "tappedDepth" : 7.6 * mm, "tapClearance" : 3, "locations" : qUnion([Q0, Q1, Q2, Q3]), "scope" : qUnion([Q4])});
        }
        {
            var Q0;
            {var subQ0=sQuery(id+"F0.wireOp",EDGE,"E22");var subQ9=sQuery(id+"F0.wireOp",EDGE,"E25");var subQ11=sQuery(id+"F0.wireOp",EDGE,"E21");Q0=makeQuery(id+"FjpGXXQrmrtnJyJ_1.boolean.opBoolean","SPLIT",FACE,{"disambiguationData":[TD([makeQuery(id+"F1.opExtrude","SWEPT_FACE",FACE,{"disambiguationData":[OSD([subQ0])]})])],"derivedFrom":makeQuery(id+"F1.opExtrude","SWEPT_FACE",FACE,{"disambiguationData":[OSD([subQ11,subQ9])]})});}
            var sketch = newSketch(context, id + "F23", { "sketchPlane" : qUnion([Q0])});
            skLineSegment(sketch, "E96", {"start": v(19.06, -4.3) * mm, "end": v(28.1, -4.3) * mm});
            skLineSegment(sketch, "E97", {"start": v(19.06, -20.7) * mm, "end": v(28.1, -20.7) * mm});
            skPoint(sketch, "E98", {"position": v(-13, -4.3) * mm});
            skPoint(sketch, "E99", {"position": v(-13, -20.7) * mm});
            skPoint(sketch, "E100", {"position": v(19.06, -4.3) * mm});
            skPoint(sketch, "E101", {"position": v(19.06, -20.7) * mm});
            skPoint(sketch, "E102.orphan", {"position": v(-10, -20.7) * mm});
            skPoint(sketch, "E103.orphan", {"position": v(-10, -4.3) * mm});
            skPoint(sketch, "E104.end.orphan", {"position": v(-16, -20.7) * mm});
            skPoint(sketch, "E105.end.orphan", {"position": v(-16, -4.3) * mm});
            skSolve(sketch);
        }
        {
            var Q0;
            Q0=sQuery(id+"F23.wireOp",VERTEX,"E98");
            var Q1;
            Q1=sQuery(id+"F23.wireOp",VERTEX,"E99");
            var Q2;
            Q2=sQuery(id+"F23.wireOp",VERTEX,"95fecb40-6dee-438e-ade6-2e9aa052387a");
            var Q3;
            Q3=sQuery(id+"F23.wireOp",VERTEX,"5c4d115d-a3d0-4a2b-9813-a859292176f2");
            var Q4;
            Q4=sQuery(id+"F23.wireOp",VERTEX,"E100");
            var Q5;
            Q5=sQuery(id+"F23.wireOp",VERTEX,"E101");
            var Q6;
            Q6=makeQuery(id+"F1.opExtrude","SWEPT_BODY",BODY,{"disambiguationData":[OSD([sQuery(id+"F0.wireOp",EDGE,"E9"),sQuery(id+"F0.wireOp",EDGE,"E10"),sQuery(id+"F0.wireOp",EDGE,"E11"),sQuery(id+"F0.wireOp",EDGE,"E12"),sQuery(id+"F0.wireOp",EDGE,"E13"),sQuery(id+"F0.wireOp",EDGE,"E14"),sQuery(id+"F0.wireOp",EDGE,"E15"),sQuery(id+"F0.wireOp",EDGE,"E16"),sQuery(id+"F0.wireOp",EDGE,"E17"),sQuery(id+"F0.wireOp",EDGE,"E18"),sQuery(id+"F0.wireOp",EDGE,"E21"),sQuery(id+"F0.wireOp",EDGE,"E22"),sQuery(id+"F0.wireOp",EDGE,"E24"),sQuery(id+"F0.wireOp",EDGE,"E25"),sQuery(id+"F0.wireOp",EDGE,"E26"),sQuery(id+"F0.wireOp",EDGE,"E27"),sQuery(id+"F0.wireOp",EDGE,"E29"),sQuery(id+"F0.wireOp",EDGE,"E30"),sQuery(id+"F0.wireOp",EDGE,"E31"),sQuery(id+"F0.wireOp",EDGE,"E32"),sQuery(id+"F0.wireOp",EDGE,"E34.filletArc"),sQuery(id+"F0.wireOp",EDGE,"E35.filletArc")])]});
            hole(context, id + "F24", {"style" : HoleStyle.SIMPLE, "endStyle" : HoleEndStyle.BLIND, "standardTappedOrClearance" : lookupTablePath({ "standard" : "ISO", "engagement" : "75%", "pitch" : "0.8 mm", "size" : "M5", "type" : "Tapped" }), "standardBlindInLast" : lookupTablePath({ "standard" : "ISO", "engagement" : "75%", "pitch" : "0.8 mm", "size" : "M5", "type" : "Tapped" }), "holeDiameter" : 4.2 * mm, "majorDiameter" : 5 * mm, "showTappedDepth" : true, "holeDepth" : 10 * mm, "isTappedThrough" : true, "tappedDepth" : 7.6 * mm, "tapClearance" : 3, "locations" : qUnion([Q0, Q1, Q2, Q3, Q4, Q5]), "scope" : qUnion([Q6])});
        }
        {
            var Q0;
            Q0=makeQuery(id+"F1.opExtrude","SWEPT_FACE",FACE,{"disambiguationData":[OSD([sQuery(id+"F0.wireOp",EDGE,"E32")])]});
            var sketch = newSketch(context, id + "F25", { "sketchPlane" : qUnion([Q0])});
            skLineSegment(sketch, "E106", {"start": v(-32.47, 0) * mm, "end": v(32.22, -25) * mm});
            skLineSegment(sketch, "E107", {"start": v(-32.47, -25) * mm, "end": v(32.22, 0) * mm});
            skPoint(sketch, "E108", {"position": v(-23.14, -21.4) * mm});
            skPoint(sketch, "E109", {"position": v(-23.14, -3.6) * mm});
            skPoint(sketch, "E110", {"position": v(32.22, -25) * mm});
            skSolve(sketch);
        }
        {
            var Q0;
            Q0=sQuery(id+"F25.wireOp",VERTEX,"E109");
            var Q1;
            Q1=sQuery(id+"F25.wireOp",VERTEX,"E108");
            var Q2;
            Q2=sQuery(id+"F25.wireOp",VERTEX,"c15fa140-9604-4616-bb4b-56b4743ac27f");
            var Q3;
            Q3=sQuery(id+"F25.wireOp",VERTEX,"ee11ad6e-ffd4-4928-85d1-b1639c15d129");
            var Q4;
            Q4=makeQuery(id+"F1.opExtrude","SWEPT_BODY",BODY,{"disambiguationData":[OSD([sQuery(id+"F0.wireOp",EDGE,"E9"),sQuery(id+"F0.wireOp",EDGE,"E10"),sQuery(id+"F0.wireOp",EDGE,"E11"),sQuery(id+"F0.wireOp",EDGE,"E12"),sQuery(id+"F0.wireOp",EDGE,"E13"),sQuery(id+"F0.wireOp",EDGE,"E14"),sQuery(id+"F0.wireOp",EDGE,"E15"),sQuery(id+"F0.wireOp",EDGE,"E16"),sQuery(id+"F0.wireOp",EDGE,"E17"),sQuery(id+"F0.wireOp",EDGE,"E18"),sQuery(id+"F0.wireOp",EDGE,"E21"),sQuery(id+"F0.wireOp",EDGE,"E22"),sQuery(id+"F0.wireOp",EDGE,"E24"),sQuery(id+"F0.wireOp",EDGE,"E25"),sQuery(id+"F0.wireOp",EDGE,"E26"),sQuery(id+"F0.wireOp",EDGE,"E27"),sQuery(id+"F0.wireOp",EDGE,"E29"),sQuery(id+"F0.wireOp",EDGE,"E30"),sQuery(id+"F0.wireOp",EDGE,"E31"),sQuery(id+"F0.wireOp",EDGE,"E32"),sQuery(id+"F0.wireOp",EDGE,"E34.filletArc"),sQuery(id+"F0.wireOp",EDGE,"E35.filletArc")])]});
            hole(context, id + "F26", {"style" : HoleStyle.SIMPLE, "endStyle" : HoleEndStyle.THROUGH, "holeDiameter" : 3.02 * mm, "majorDiameter" : 5 * mm, "isTappedThrough" : true, "tappedDepth" : 7.6 * mm, "tapClearance" : 3, "locations" : qUnion([Q0, Q1, Q2, Q3]), "scope" : qUnion([Q4])});
        }
        {
            var Q0;
            Q0=makeQuery(id+"F1.opExtrude","SWEPT_FACE",FACE,{"disambiguationData":[OSD([sQuery(id+"F0.wireOp",EDGE,"E26")])]});
            var sketch = newSketch(context, id + "F27", { "sketchPlane" : qUnion([Q0])});
            skLineSegment(sketch, "E111", {"start": v(-32.59, 0) * mm, "end": v(32.59, -25) * mm});
            skLineSegment(sketch, "E112", {"start": v(-32.59, -25) * mm, "end": v(32.59, 0) * mm});
            skPoint(sketch, "E113", {"position": v(23.25, -3.58) * mm});
            skPoint(sketch, "E114", {"position": v(23.25, -21.42) * mm});
            skSolve(sketch);
        }
        {
            var Q0;
            Q0=sQuery(id+"F27.wireOp",VERTEX,"2f9b4e08-407a-4854-a18f-1e0d48b055ba");
            var Q1;
            Q1=sQuery(id+"F27.wireOp",VERTEX,"d0e48b6c-0c36-4a9f-8b0d-3dbf71a8332a");
            var Q2;
            Q2=sQuery(id+"F27.wireOp",VERTEX,"E113");
            var Q3;
            Q3=sQuery(id+"F27.wireOp",VERTEX,"E114");
            var Q4;
            Q4=makeQuery(id+"F1.opExtrude","SWEPT_BODY",BODY,{"disambiguationData":[OSD([sQuery(id+"F0.wireOp",EDGE,"E9"),sQuery(id+"F0.wireOp",EDGE,"E10"),sQuery(id+"F0.wireOp",EDGE,"E11"),sQuery(id+"F0.wireOp",EDGE,"E12"),sQuery(id+"F0.wireOp",EDGE,"E13"),sQuery(id+"F0.wireOp",EDGE,"E14"),sQuery(id+"F0.wireOp",EDGE,"E15"),sQuery(id+"F0.wireOp",EDGE,"E16"),sQuery(id+"F0.wireOp",EDGE,"E17"),sQuery(id+"F0.wireOp",EDGE,"E18"),sQuery(id+"F0.wireOp",EDGE,"E21"),sQuery(id+"F0.wireOp",EDGE,"E22"),sQuery(id+"F0.wireOp",EDGE,"E24"),sQuery(id+"F0.wireOp",EDGE,"E25"),sQuery(id+"F0.wireOp",EDGE,"E26"),sQuery(id+"F0.wireOp",EDGE,"E27"),sQuery(id+"F0.wireOp",EDGE,"E29"),sQuery(id+"F0.wireOp",EDGE,"E30"),sQuery(id+"F0.wireOp",EDGE,"E31"),sQuery(id+"F0.wireOp",EDGE,"E32"),sQuery(id+"F0.wireOp",EDGE,"E34.filletArc"),sQuery(id+"F0.wireOp",EDGE,"E35.filletArc")])]});
            hole(context, id + "F28", {"style" : HoleStyle.SIMPLE, "endStyle" : HoleEndStyle.THROUGH, "holeDiameter" : 3.02 * mm, "majorDiameter" : 5 * mm, "isTappedThrough" : true, "tappedDepth" : 7.6 * mm, "tapClearance" : 3, "locations" : qUnion([Q0, Q1, Q2, Q3]), "scope" : qUnion([Q4])});
        }
    });
